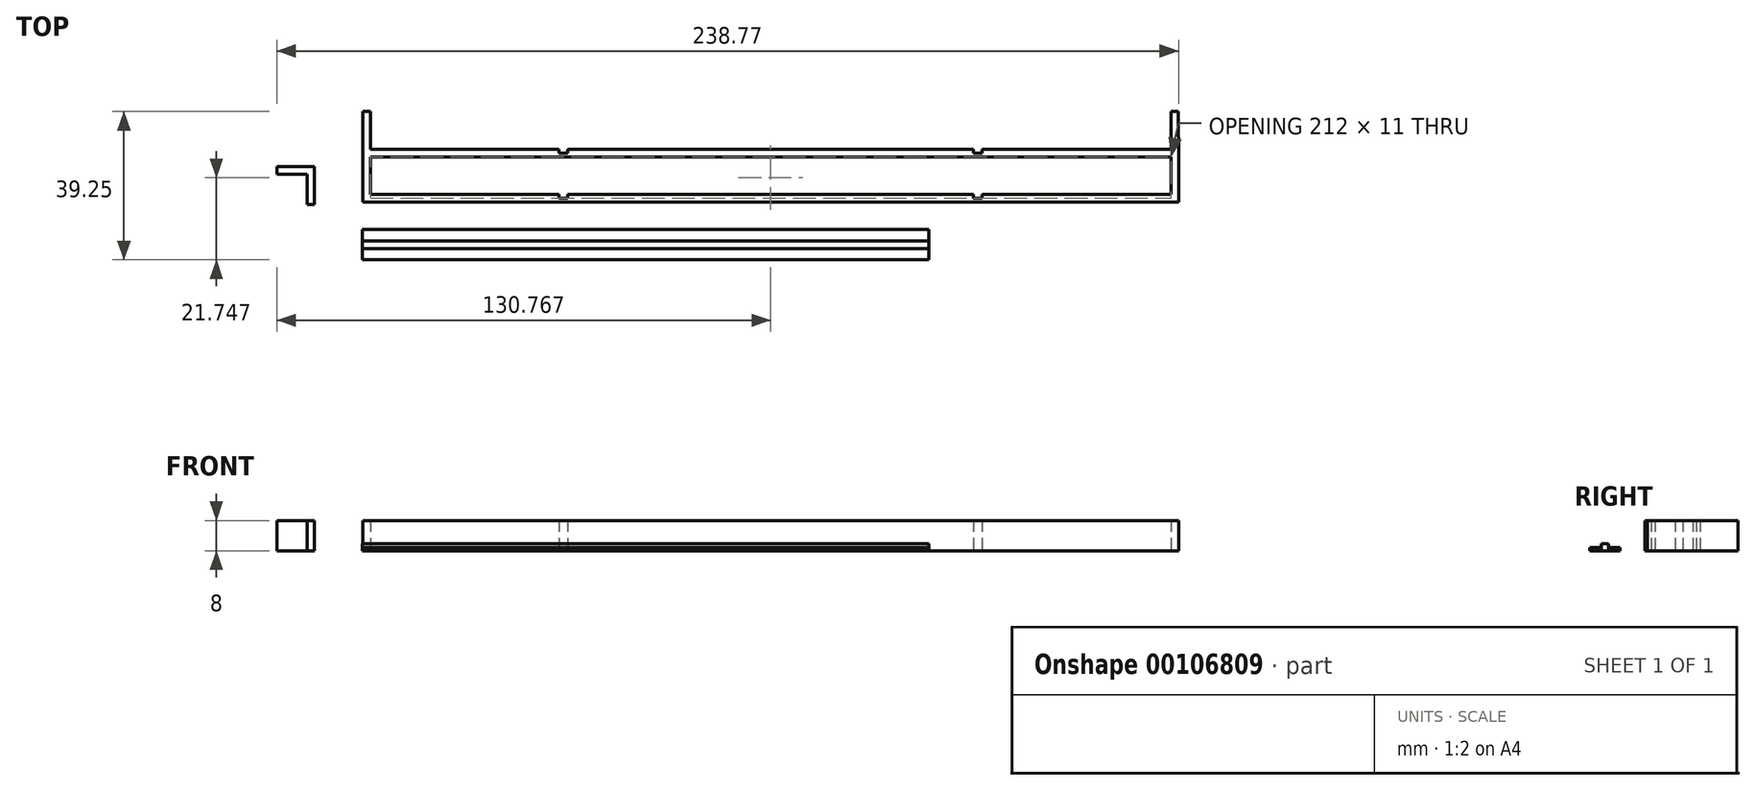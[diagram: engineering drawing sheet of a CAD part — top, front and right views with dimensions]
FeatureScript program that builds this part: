
annotation { "Feature Type Name" : "Feature", "Feature Type Description" : "" }
export const myFeature = defineFeature(function(context is Context, id is Id, definition is map)
    precondition{}
    {
        {
            var Q0;
            Q0=qCreatedBy(makeId("Top.planeOp"),FACE);
            var sketch = newSketch(context, id + "F0", { "sketchPlane" : qUnion([Q0])});
            skLineSegment(sketch, "E0.bottom", {"start": v(-38.01, 29.77) * mm, "end": v(11.99, 29.77) * mm});
            skLineSegment(sketch, "E0.top", {"start": v(-38.01, 39.77) * mm, "end": v(173.99, 39.77) * mm});
            skLineSegment(sketch, "E0.left", {"start": v(-38.01, 39.77) * mm, "end": v(-38.01, 29.77) * mm});
            skLineSegment(sketch, "E0.right", {"start": v(173.99, 39.77) * mm, "end": v(173.99, 29.77) * mm});
            skLineSegment(sketch, "E1", {"start": v(-40.01, 51.77) * mm, "end": v(-40.01, 27.77) * mm});
            skLineSegment(sketch, "E2", {"start": v(-40.01, 27.77) * mm, "end": v(175.99, 27.77) * mm});
            skLineSegment(sketch, "E3", {"start": v(175.99, 27.77) * mm, "end": v(175.99, 38.23) * mm});
            skLineSegment(sketch, "E4", {"start": v(173.99, 41.77) * mm, "end": v(173.99, 38.23) * mm});
            skLineSegment(sketch, "E5", {"start": v(173.99, 41.77) * mm, "end": v(123.99, 41.77) * mm});
            skLineSegment(sketch, "E6", {"start": v(-38.01, 41.77) * mm, "end": v(-38.01, 51.77) * mm});
            skLineSegment(sketch, "E7", {"start": v(-38.01, 51.77) * mm, "end": v(-40.01, 51.77) * mm});
            skLineSegment(sketch, "E8", {"start": v(-62.78, 37.15) * mm, "end": v(-62.78, 35.15) * mm});
            skLineSegment(sketch, "E9", {"start": v(-62.78, 35.15) * mm, "end": v(-54.78, 35.15) * mm});
            skLineSegment(sketch, "E10", {"start": v(-54.78, 35.15) * mm, "end": v(-54.78, 27.15) * mm});
            skLineSegment(sketch, "E11", {"start": v(-54.78, 27.15) * mm, "end": v(-52.78, 27.15) * mm});
            skLineSegment(sketch, "E12", {"start": v(-52.78, 27.15) * mm, "end": v(-52.78, 37.15) * mm});
            skLineSegment(sketch, "E13", {"start": v(-52.78, 37.15) * mm, "end": v(-62.78, 37.15) * mm});
            skLineSegment(sketch, "E14.bottom", {"start": v(-40.18, 17.52) * mm, "end": v(109.82, 17.52) * mm});
            skLineSegment(sketch, "E14.top", {"start": v(-40.18, 15.52) * mm, "end": v(109.82, 15.52) * mm});
            skLineSegment(sketch, "E14.left", {"start": v(-40.18, 17.52) * mm, "end": v(-40.18, 15.52) * mm});
            skLineSegment(sketch, "E14.right", {"start": v(109.82, 17.52) * mm, "end": v(109.82, 15.52) * mm});
            skLineSegment(sketch, "E15", {"start": v(173.99, 41.77) * mm, "end": v(173.99, 51.77) * mm});
            skLineSegment(sketch, "E16", {"start": v(173.99, 51.77) * mm, "end": v(175.95, 51.77) * mm});
            skLineSegment(sketch, "E17", {"start": v(175.95, 51.77) * mm, "end": v(175.99, 38.23) * mm});
            skLineSegment(sketch, "E18", {"start": v(11.99, 41.77) * mm, "end": v(11.99, 40.77) * mm});
            skLineSegment(sketch, "E19", {"start": v(11.99, 40.77) * mm, "end": v(14.29, 40.77) * mm});
            skLineSegment(sketch, "E20", {"start": v(14.29, 40.77) * mm, "end": v(14.29, 41.77) * mm});
            skLineSegment(sketch, "E21", {"start": v(11.99, 29.77) * mm, "end": v(11.99, 28.77) * mm});
            skLineSegment(sketch, "E22", {"start": v(11.99, 28.77) * mm, "end": v(14.29, 28.77) * mm});
            skLineSegment(sketch, "E23", {"start": v(14.29, 28.77) * mm, "end": v(14.29, 29.77) * mm});
            skLineSegment(sketch, "E24", {"start": v(121.69, 41.77) * mm, "end": v(121.69, 40.77) * mm});
            skLineSegment(sketch, "E25", {"start": v(121.69, 40.77) * mm, "end": v(123.99, 40.77) * mm});
            skLineSegment(sketch, "E26", {"start": v(123.99, 40.77) * mm, "end": v(123.99, 41.77) * mm});
            skLineSegment(sketch, "E27", {"start": v(121.69, 29.77) * mm, "end": v(121.69, 28.77) * mm});
            skLineSegment(sketch, "E28", {"start": v(121.69, 28.77) * mm, "end": v(123.99, 28.77) * mm});
            skLineSegment(sketch, "E29", {"start": v(123.99, 28.77) * mm, "end": v(123.99, 29.77) * mm});
            skLineSegment(sketch, "E30.trimOffspring", {"start": v(121.69, 41.77) * mm, "end": v(14.29, 41.77) * mm});
            skLineSegment(sketch, "E31.trimOffspring", {"start": v(123.99, 29.77) * mm, "end": v(173.99, 29.77) * mm});
            skLineSegment(sketch, "E32.trimOffspring", {"start": v(14.29, 29.77) * mm, "end": v(121.69, 29.77) * mm});
            skLineSegment(sketch, "E33.trimOffspring", {"start": v(11.99, 41.77) * mm, "end": v(-38.01, 41.77) * mm});
            skLineSegment(sketch, "E34", {"start": v(-30.2, -15.5) * mm, "end": v(-12.2, -15.5) * mm});
            skLineSegment(sketch, "E35", {"start": v(-36.2, -23.84) * mm, "end": v(-6.2, -23.84) * mm});
            skLineSegment(sketch, "E36", {"start": v(-36.2, -23.84) * mm, "end": v(-30.2, -15.5) * mm});
            skLineSegment(sketch, "E37", {"start": v(-30.2, -15.5) * mm, "end": v(-21.2, -2.97) * mm});
            skLineSegment(sketch, "E38", {"start": v(-6.2, -23.84) * mm, "end": v(-12.2, -15.5) * mm});
            skLineSegment(sketch, "E39", {"start": v(-48.6, -17.34) * mm, "end": v(-36.2, -23.84) * mm});
            skLineSegment(sketch, "E40", {"start": v(6.2, -17.34) * mm, "end": v(-6.2, -23.84) * mm});
            skLineSegment(sketch, "E41", {"start": v(0.2, -9) * mm, "end": v(-12.2, -15.5) * mm});
            skLineSegment(sketch, "E42", {"start": v(-42.61, -9) * mm, "end": v(-30.2, -15.5) * mm});
            skLineSegment(sketch, "E43", {"start": v(-42.61, -9) * mm, "end": v(-48.6, -17.34) * mm});
            skLineSegment(sketch, "E44", {"start": v(6.2, -17.34) * mm, "end": v(0.2, -9) * mm});
            skLineSegment(sketch, "E45", {"start": v(-21.2, -0.48) * mm, "end": v(-21.2, -17.2) * mm});
            skLineSegment(sketch, "E46", {"start": v(-21.2, -0.48) * mm, "end": v(-21.2, 11.75) * mm});
            skLineSegment(sketch, "E47", {"start": v(-21.2, -2.97) * mm, "end": v(-12.2, -15.5) * mm});
            skLineSegment(sketch, "E48", {"start": v(-40.18, 15.52) * mm, "end": v(-40.18, 12.52) * mm});
            skLineSegment(sketch, "E49", {"start": v(-40.18, 12.52) * mm, "end": v(109.82, 12.52) * mm});
            skLineSegment(sketch, "E50", {"start": v(109.82, 12.52) * mm, "end": v(109.82, 15.52) * mm});
            skLineSegment(sketch, "E51", {"start": v(-40.18, 17.52) * mm, "end": v(-40.18, 20.52) * mm});
            skLineSegment(sketch, "E52", {"start": v(-40.18, 20.52) * mm, "end": v(109.82, 20.52) * mm});
            skLineSegment(sketch, "E53", {"start": v(109.82, 20.52) * mm, "end": v(109.82, 17.52) * mm});
            skSolve(sketch);
        }
        {
            var Q0;
            Q0=makeQuery(id+"F0.imprint","IMPRINT",FACE,{"disambiguationData":[TD([[makeQuery(id+"F0.imprint","IMPRINT",EDGE,{"derivedFrom":sQuery(id+"F0.wireOp",EDGE,"E8")}),1.0]])]});
            var Q1;
            Q1=makeQuery(id+"F0.imprint","IMPRINT",FACE,{"disambiguationData":[TD([[makeQuery(id+"F0.imprint","IMPRINT",EDGE,{"derivedFrom":sQuery(id+"F0.wireOp",EDGE,"E0.bottom")}),-1.0]])]});
            extrude(context, id + "F1", {"entities" : qUnion([Q0, Q1]), "depth" : 8 * mm});
        }
        {
            var Q0;
            Q0=makeQuery(id+"F0.imprint","IMPRINT",FACE,{"disambiguationData":[TD([[makeQuery(id+"F0.imprint","IMPRINT",EDGE,{"derivedFrom":sQuery(id+"F0.wireOp",EDGE,"E14.top")}),-1.0]])]});
            var Q1;
            Q1=makeQuery(id+"F0.imprint","IMPRINT",FACE,{"disambiguationData":[TD([[makeQuery(id+"F0.imprint","IMPRINT",EDGE,{"derivedFrom":sQuery(id+"F0.wireOp",EDGE,"E14.bottom")}),1.0]])]});
            extrude(context, id + "F2", {"entities" : qUnion([Q0, Q1]), "depth" : 0.8 * mm});
        }
        {
            var Q0;
            Q0=makeQuery(id+"F0.imprint","IMPRINT",FACE,{"disambiguationData":[TD([[makeQuery(id+"F0.imprint","IMPRINT",EDGE,{"derivedFrom":sQuery(id+"F0.wireOp",EDGE,"E14.bottom")}),-1.0]])]});
            extrude(context, id + "F3", {"entities" : qUnion([Q0]), "depth" : 1.8 * mm});
        }
    });
